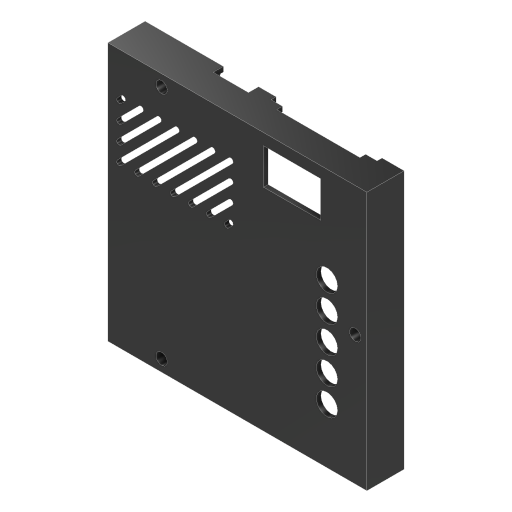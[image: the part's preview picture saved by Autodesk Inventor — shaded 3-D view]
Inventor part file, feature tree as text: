
AUTODESK INVENTOR PART (.ipt)
format: ipt  version: 2023 (Build 270158000, 158)  size: 849,408 bytes
history: native  units: mm
features: sketch x12, extrude x9, projected_geometry x8, hole x3, other x1
ambient origin geometry x8: Origin, YZ Plane, XZ Plane, XY Plane, X Axis, Y Axis, Z Axis, Center Point
bodies: Body1 (feature_tree)
feature tree (33):
  other  "Těleso1"
  extrude  "Vysunutí1"  Depth=158.75mm
  extrude  "Vysunutí2"  Depth=158.5mm
  extrude  "Vysunutí3"  Depth=2.8mm TaperAngle=0.0deg
  extrude  "Vysunutí4"  Depth=3.0mm
  extrude  "Vysunutí5"  Depth=4.0mm
  extrude  "Vysunutí6"  Depth=4.0mm
  hole  "Díra1"  [1 undecoded]
  hole  "Díra2"  [1 undecoded]
  extrude  "Vysunutí7"  Depth=28.5mm
  hole  "Díra3"  [1 undecoded]
  extrude  "Vysunutí8"  Depth=28.5mm
  extrude  "Vysunutí9"  Depth=14.25mm
  sketch  "Náčrt1"
  sketch  "Náčrt2"
  projected_geometry  "Promítnutá smyčka1"
  sketch  "Náčrt3"
  projected_geometry  "Promítnutá smyčka2"
  sketch  "Náčrt4"
  projected_geometry  "Promítnutá smyčka3"
  sketch  "Náčrt5"
  projected_geometry  "Promítnutá smyčka4"
  sketch  "Náčrt6"
  projected_geometry  "Promítnutá smyčka5"
  sketch  "Náčrt7"
  projected_geometry  "Promítnutá smyčka6"
  sketch  "Náčrt8"
  sketch  "Náčrt9"
  projected_geometry  "Promítnutá smyčka7"
  sketch  "Náčrt10"
  projected_geometry  "Promítnutá smyčka8"
  sketch  "Náčrt11"
  sketch  "Náčrt12"
note: 3 required parameter values undecoded (feature->parameter linkage not recoverable at this tier; creation-order binding heuristic only, values carry confidence <= 0.55)
